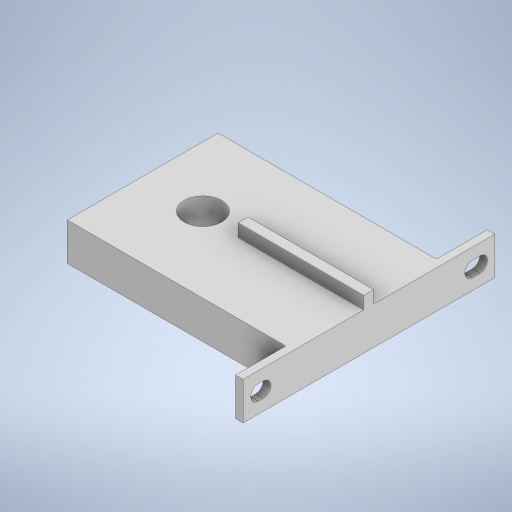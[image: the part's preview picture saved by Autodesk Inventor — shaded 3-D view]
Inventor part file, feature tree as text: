
AUTODESK INVENTOR PART (.ipt)
format: ipt  version: 2023 (Build 270158000, 158)  size: 297,472 bytes
history: native  units: mm
features: other x3, extrude x3, sketch x3
ambient origin geometry x8: Origin, YZ Plane, XZ Plane, XY Plane, X Axis, Y Axis, Z Axis, Center Point
bodies: Body1 (feature_tree)
feature tree (9):
  other  "Твердое тело1"
  extrude  "Выдавливание1"  Depth=90.0mm
  other  "РабПлоскость3"
  extrude  "Выдавливание3"  Depth=60.0mm
  other  "РабПлоскость1"
  sketch  "Эскиз6"
  extrude  "Выдавливание7"  Depth=15.0mm TaperAngle=0.0deg
  sketch  "Эскиз3"
  sketch  "Эскиз7"
